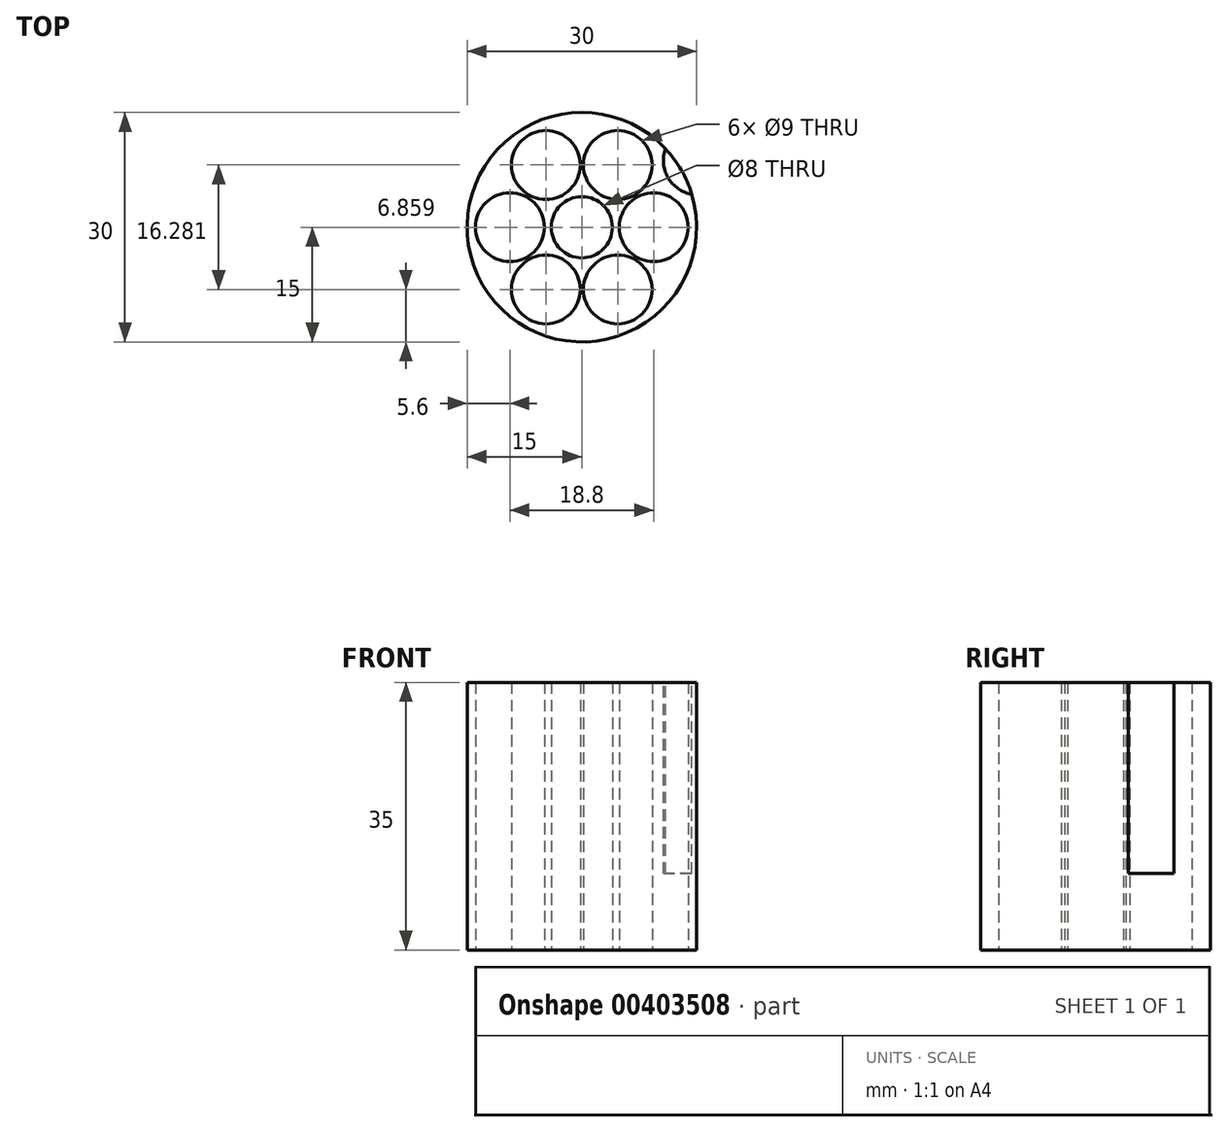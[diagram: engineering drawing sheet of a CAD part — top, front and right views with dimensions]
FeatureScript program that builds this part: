
annotation { "Feature Type Name" : "Feature", "Feature Type Description" : "" }
export const myFeature = defineFeature(function(context is Context, id is Id, definition is map)
    precondition{}
    {
        {
            var Q0;
            Q0=qCreatedBy(makeId("Top.planeOp"),FACE);
            var sketch = newSketch(context, id + "F0", { "sketchPlane" : qUnion([Q0])});
            skCircle(sketch, "E0", {"center": v(0, 0) * mm, "radius": 15 * mm});
            skCircle(sketch, "E1", {"center": v(0, 0) * mm, "radius": 4 * mm});
            skLineSegment(sketch, "E2", {"start": v(-15, 0) * mm, "end": v(15, 0) * mm, "construction": true});
            skCircle(sketch, "E3", {"center": v(9.4, 0) * mm, "radius": 4.5 * mm});
            skCircle(sketch, "E4.1.0", {"center": v(4.7, 8.14) * mm, "radius": 4.5 * mm});
            skCircle(sketch, "E4.2.0", {"center": v(-4.7, 8.14) * mm, "radius": 4.5 * mm});
            skCircle(sketch, "E4.3.0", {"center": v(-9.4, 0) * mm, "radius": 4.5 * mm});
            skCircle(sketch, "E4.4.0", {"center": v(-4.7, -8.14) * mm, "radius": 4.5 * mm});
            skCircle(sketch, "E4.5.0", {"center": v(4.7, -8.14) * mm, "radius": 4.5 * mm});
            skSolve(sketch);
        }
        {
            var Q0;
            Q0 = qSketchRegion(id + "F0", true);
            extrude(context, id + "F1", {"entities" : qUnion([Q0]), "depth" : 35 * mm});
        }
        {
            var Q0;
            Q0=makeQuery(id+"F1.opExtrude","CAP_FACE",FACE,{"disambiguationData":[OSD([sQuery(id+"F0.wireOp",EDGE,"E0"),sQuery(id+"F0.wireOp",EDGE,"E1"),sQuery(id+"F0.wireOp",EDGE,"E3"),sQuery(id+"F0.wireOp",EDGE,"E4.1.0"),sQuery(id+"F0.wireOp",EDGE,"E4.2.0"),sQuery(id+"F0.wireOp",EDGE,"E4.3.0"),sQuery(id+"F0.wireOp",EDGE,"E4.4.0"),sQuery(id+"F0.wireOp",EDGE,"E4.5.0")])],"isStart":false});
            var sketch = newSketch(context, id + "F2", { "sketchPlane" : qUnion([Q0])});
            skCircle(sketch, "E5", {"center": v(15.16, 8.75) * mm, "radius": 4.5 * mm});
            skLineSegment(sketch, "E6", {"start": v(0, 0) * mm, "end": v(15.16, 8.75) * mm, "construction": true});
            skLineSegment(sketch, "E7", {"start": v(0, 0) * mm, "end": v(19.9, 0) * mm, "construction": true});
            skSolve(sketch);
        }
        {
            var Q0;
            {var subQ0=sQuery(id+"F2.wireOp",EDGE,"E5");var subQ1=makeQuery(id+"F1.opExtrude","CAP_EDGE",EDGE,{"disambiguationData":[OSD([sQuery(id+"F0.wireOp",EDGE,"E0")])],"isStart":false});var subQ2=makeQuery(id+"F2.imprint","INTERSECT",VERTEX,{"disambiguationData":[OD(0.0)],"derivedFrom":[subQ1,subQ0]});Q0=makeQuery(id+"F2.imprint","IMPRINT",FACE,{"disambiguationData":[TD([[makeQuery(id+"F2.imprint","IMPRINT",EDGE,{"disambiguationData":[TD([[subQ2,-1.0]])],"derivedFrom":subQ0}),1.0]])]});}
            extrude(context, id + "F3", {"entities" : qUnion([Q0]), "operationType" : NewBodyOperationType.REMOVE, "oppositeDirection" : true, "depth" : 25 * mm});
        }
    });
